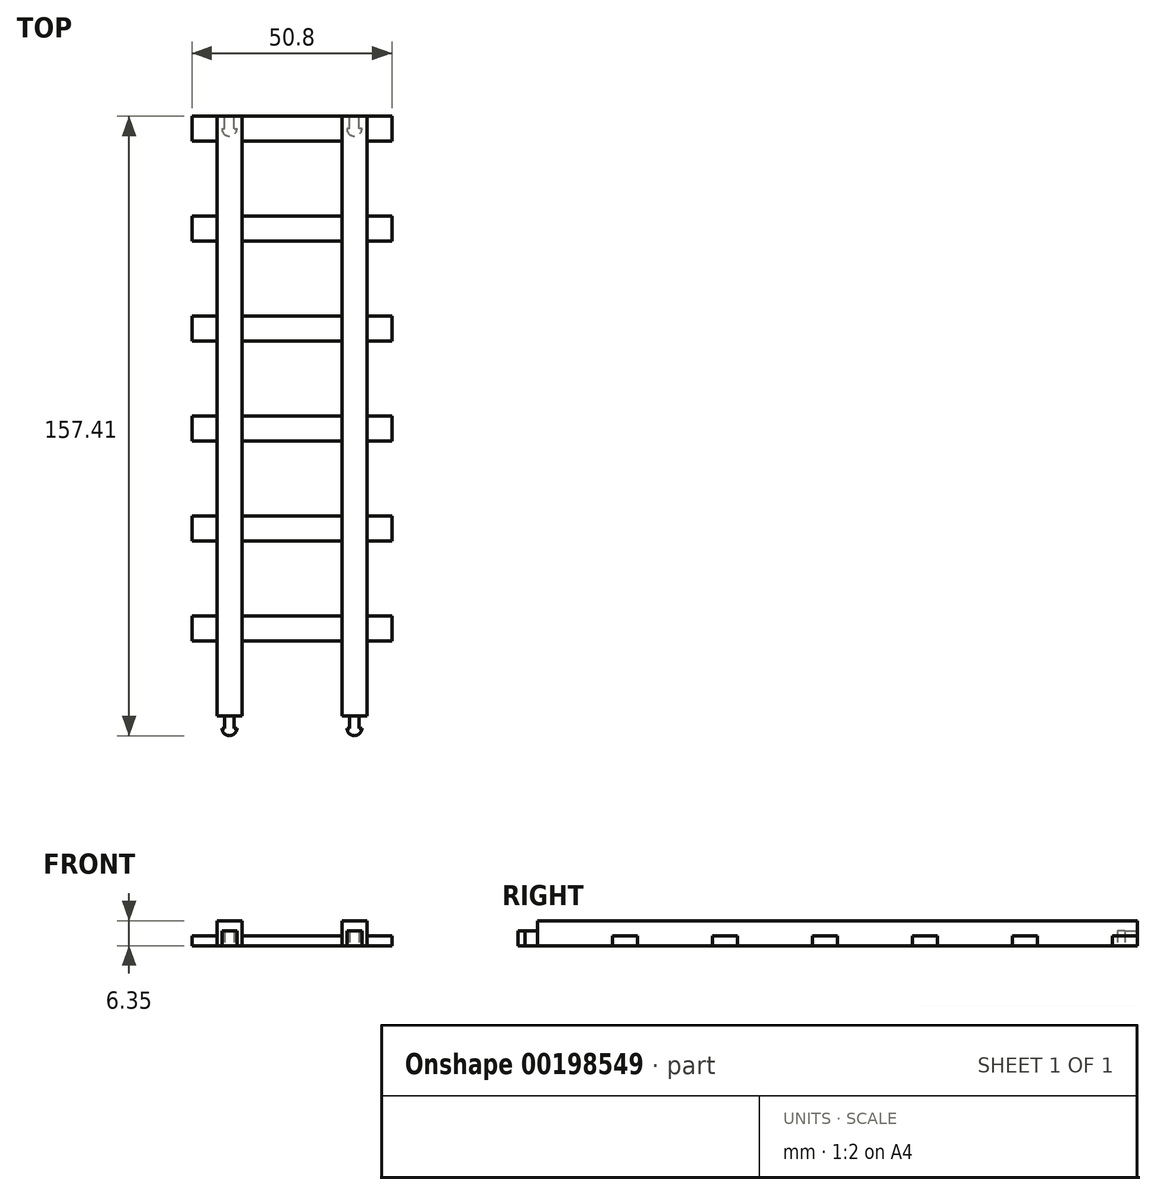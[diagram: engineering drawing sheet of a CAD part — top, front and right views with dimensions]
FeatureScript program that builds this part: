
annotation { "Feature Type Name" : "Feature", "Feature Type Description" : "" }
export const myFeature = defineFeature(function(context is Context, id is Id, definition is map)
    precondition{}
    {
        {
            var Q0;
            Q0=qCreatedBy(makeId("Top.planeOp"),FACE);
            var sketch = newSketch(context, id + "F0", { "sketchPlane" : qUnion([Q0])});
            skLineSegment(sketch, "E0.bottom", {"start": v(25.4, 76.2) * mm, "end": v(-25.4, 76.2) * mm, "construction": true});
            skLineSegment(sketch, "E0.top", {"start": v(25.4, -76.2) * mm, "end": v(-25.4, -76.2) * mm, "construction": true});
            skLineSegment(sketch, "E0.left", {"start": v(25.4, 76.2) * mm, "end": v(25.4, -76.2) * mm, "construction": true});
            skLineSegment(sketch, "E0.right", {"start": v(-25.4, 76.2) * mm, "end": v(-25.4, -76.2) * mm, "construction": true});
            skPoint(sketch, "E0.middle", {"position": v(0, 0) * mm});
            skLineSegment(sketch, "E1", {"start": v(-25.4, -76.2) * mm, "end": v(-19.05, -76.2) * mm, "construction": true});
            skLineSegment(sketch, "E2", {"start": v(-19.05, -76.2) * mm, "end": v(-19.05, 76.2) * mm});
            skLineSegment(sketch, "E3.MirrorCS", {"start": v(19.05, -76.2) * mm, "end": v(19.05, 76.2) * mm});
            skLineSegment(sketch, "E4", {"start": v(-25.4, -76.2) * mm, "end": v(-12.7, -76.2) * mm, "construction": true});
            skLineSegment(sketch, "E5", {"start": v(-12.7, -76.2) * mm, "end": v(-12.7, 76.2) * mm});
            skLineSegment(sketch, "E6.MirrorCS", {"start": v(12.7, -76.2) * mm, "end": v(12.7, 76.2) * mm});
            skLineSegment(sketch, "E7", {"start": v(-19.05, 76.2) * mm, "end": v(-12.7, 76.2) * mm});
            skLineSegment(sketch, "E8", {"start": v(12.7, 76.2) * mm, "end": v(19.05, 76.2) * mm});
            skLineSegment(sketch, "E9", {"start": v(-19.05, -76.2) * mm, "end": v(-12.7, -76.2) * mm});
            skLineSegment(sketch, "E10", {"start": v(12.7, -76.2) * mm, "end": v(19.05, -76.2) * mm});
            skSolve(sketch);
        }
        {
            var Q0;
            Q0 = qSketchRegion(id + "F0", true);
            extrude(context, id + "F1", {"entities" : qUnion([Q0]), "depth" : 6.35 * mm});
        }
        {
            var Q0;
            Q0=qCreatedBy(makeId("Top.planeOp"),FACE);
            var sketch = newSketch(context, id + "F2", { "sketchPlane" : qUnion([Q0])});
            skLineSegment(sketch, "E11.bottom", {"start": v(-25.4, -76.2) * mm, "end": v(25.4, -76.2) * mm, "construction": true});
            skLineSegment(sketch, "E11.top", {"start": v(-25.4, 76.2) * mm, "end": v(25.4, 76.2) * mm, "construction": true});
            skLineSegment(sketch, "E11.left", {"start": v(-25.4, -76.2) * mm, "end": v(-25.4, 76.2) * mm, "construction": true});
            skLineSegment(sketch, "E11.right", {"start": v(25.4, -76.2) * mm, "end": v(25.4, 76.2) * mm, "construction": true});
            skPoint(sketch, "E11.middle", {"position": v(0, 0) * mm});
            skLineSegment(sketch, "E12", {"start": v(-25.4, -76.2) * mm, "end": v(-25.4, -50.8) * mm, "construction": true});
            skLineSegment(sketch, "E13", {"start": v(-25.4, -76.2) * mm, "end": v(-25.4, -57.15) * mm, "construction": true});
            skLineSegment(sketch, "E14", {"start": v(-25.4, -57.15) * mm, "end": v(-25.4, -50.8) * mm});
            skLineSegment(sketch, "E15", {"start": v(-25.4, -50.8) * mm, "end": v(25.4, -50.8) * mm});
            skLineSegment(sketch, "E16", {"start": v(25.4, -50.8) * mm, "end": v(25.4, -57.15) * mm});
            skLineSegment(sketch, "E17", {"start": v(-25.4, -57.15) * mm, "end": v(25.4, -57.15) * mm});
            skLineSegment(sketch, "E18.0.1.0", {"start": v(-25.4, -25.4) * mm, "end": v(25.4, -25.4) * mm});
            skLineSegment(sketch, "E18.0.1.1", {"start": v(-25.4, -31.75) * mm, "end": v(25.4, -31.75) * mm});
            skLineSegment(sketch, "E18.0.1.2", {"start": v(25.4, -25.4) * mm, "end": v(25.4, -31.75) * mm});
            skLineSegment(sketch, "E18.0.1.3", {"start": v(-25.4, -31.75) * mm, "end": v(-25.4, -25.4) * mm});
            skLineSegment(sketch, "E18.0.2.0", {"start": v(-25.4, 0) * mm, "end": v(25.4, 0) * mm});
            skLineSegment(sketch, "E18.0.2.1", {"start": v(-25.4, -6.35) * mm, "end": v(25.4, -6.35) * mm});
            skLineSegment(sketch, "E18.0.2.2", {"start": v(25.4, 0) * mm, "end": v(25.4, -6.35) * mm});
            skLineSegment(sketch, "E18.0.2.3", {"start": v(-25.4, -6.35) * mm, "end": v(-25.4, 0) * mm});
            skLineSegment(sketch, "E18.0.3.0", {"start": v(-25.4, 25.4) * mm, "end": v(25.4, 25.4) * mm});
            skLineSegment(sketch, "E18.0.3.1", {"start": v(-25.4, 19.05) * mm, "end": v(25.4, 19.05) * mm});
            skLineSegment(sketch, "E18.0.3.2", {"start": v(25.4, 25.4) * mm, "end": v(25.4, 19.05) * mm});
            skLineSegment(sketch, "E18.0.3.3", {"start": v(-25.4, 19.05) * mm, "end": v(-25.4, 25.4) * mm});
            skLineSegment(sketch, "E18.0.4.0", {"start": v(-25.4, 50.8) * mm, "end": v(25.4, 50.8) * mm});
            skLineSegment(sketch, "E18.0.4.1", {"start": v(-25.4, 44.45) * mm, "end": v(25.4, 44.45) * mm});
            skLineSegment(sketch, "E18.0.4.2", {"start": v(25.4, 50.8) * mm, "end": v(25.4, 44.45) * mm});
            skLineSegment(sketch, "E18.0.4.3", {"start": v(-25.4, 44.45) * mm, "end": v(-25.4, 50.8) * mm});
            skLineSegment(sketch, "E18.0.5.0", {"start": v(-25.4, 76.2) * mm, "end": v(25.4, 76.2) * mm});
            skLineSegment(sketch, "E18.0.5.1", {"start": v(-25.4, 69.85) * mm, "end": v(25.4, 69.85) * mm});
            skLineSegment(sketch, "E18.0.5.2", {"start": v(25.4, 76.2) * mm, "end": v(25.4, 69.85) * mm});
            skLineSegment(sketch, "E18.0.5.3", {"start": v(-25.4, 69.85) * mm, "end": v(-25.4, 76.2) * mm});
            skLineSegment(sketch, "E18.direction1", {"start": v(-25.4, -50.8) * mm, "end": v(0, -50.8) * mm, "construction": true});
            skLineSegment(sketch, "E18.direction2", {"start": v(-25.4, -50.8) * mm, "end": v(-25.4, -25.4) * mm, "construction": true});
            skSolve(sketch);
        }
        {
            var Q0;
            Q0 = qSketchRegion(id + "F2", true);
            extrude(context, id + "F3", {"entities" : qUnion([Q0]), "operationType" : NewBodyOperationType.ADD, "depth" : 2.54 * mm});
        }
        {
            var Q0;
            Q0=makeQuery(id+"F3.boolean.opBoolean","MERGE",FACE,{"derivedFrom":[makeQuery(id+"F1.opExtrude","CAP_FACE",FACE,{"disambiguationData":[OSD([sQuery(id+"F0.wireOp",EDGE,"E2"),sQuery(id+"F0.wireOp",EDGE,"E5"),sQuery(id+"F0.wireOp",EDGE,"E7"),sQuery(id+"F0.wireOp",EDGE,"E9")])],"isStart":true}),makeQuery(id+"F1.opExtrude","CAP_FACE",FACE,{"disambiguationData":[OSD([sQuery(id+"F0.wireOp",EDGE,"E3.MirrorCS"),sQuery(id+"F0.wireOp",EDGE,"E6.MirrorCS"),sQuery(id+"F0.wireOp",EDGE,"E8"),sQuery(id+"F0.wireOp",EDGE,"E10")])],"isStart":true}),makeQuery(id+"F3.opExtrude","CAP_FACE",FACE,{"disambiguationData":[OSD([sQuery(id+"F2.wireOp",EDGE,"E14"),sQuery(id+"F2.wireOp",EDGE,"E15"),sQuery(id+"F2.wireOp",EDGE,"E16"),sQuery(id+"F2.wireOp",EDGE,"E17")])],"isStart":true}),makeQuery(id+"F3.opExtrude","CAP_FACE",FACE,{"disambiguationData":[OSD([sQuery(id+"F2.wireOp",EDGE,"E18.0.1.0"),sQuery(id+"F2.wireOp",EDGE,"E18.0.1.1"),sQuery(id+"F2.wireOp",EDGE,"E18.0.1.2"),sQuery(id+"F2.wireOp",EDGE,"E18.0.1.3")])],"isStart":true}),makeQuery(id+"F3.opExtrude","CAP_FACE",FACE,{"disambiguationData":[OSD([sQuery(id+"F2.wireOp",EDGE,"E18.0.2.0"),sQuery(id+"F2.wireOp",EDGE,"E18.0.2.1"),sQuery(id+"F2.wireOp",EDGE,"E18.0.2.2"),sQuery(id+"F2.wireOp",EDGE,"E18.0.2.3")])],"isStart":true}),makeQuery(id+"F3.opExtrude","CAP_FACE",FACE,{"disambiguationData":[OSD([sQuery(id+"F2.wireOp",EDGE,"E18.0.3.0"),sQuery(id+"F2.wireOp",EDGE,"E18.0.3.1"),sQuery(id+"F2.wireOp",EDGE,"E18.0.3.2"),sQuery(id+"F2.wireOp",EDGE,"E18.0.3.3")])],"isStart":true}),makeQuery(id+"F3.opExtrude","CAP_FACE",FACE,{"disambiguationData":[OSD([sQuery(id+"F2.wireOp",EDGE,"E18.0.4.0"),sQuery(id+"F2.wireOp",EDGE,"E18.0.4.1"),sQuery(id+"F2.wireOp",EDGE,"E18.0.4.2"),sQuery(id+"F2.wireOp",EDGE,"E18.0.4.3")])],"isStart":true}),makeQuery(id+"F3.opExtrude","CAP_FACE",FACE,{"disambiguationData":[OSD([sQuery(id+"F2.wireOp",EDGE,"E18.0.5.0"),sQuery(id+"F2.wireOp",EDGE,"E18.0.5.1"),sQuery(id+"F2.wireOp",EDGE,"E18.0.5.2"),sQuery(id+"F2.wireOp",EDGE,"E18.0.5.3")])],"isStart":true})]});
            var sketch = newSketch(context, id + "F4", { "sketchPlane" : qUnion([Q0])});
            skLineSegment(sketch, "E19", {"start": v(19.05, -76.2) * mm, "end": v(19.05, -69.85) * mm, "construction": true});
            skLineSegment(sketch, "E20", {"start": v(19.05, -69.85) * mm, "end": v(12.7, -69.85) * mm, "construction": true});
            skLineSegment(sketch, "E21", {"start": v(12.7, -69.85) * mm, "end": v(12.7, -76.2) * mm, "construction": true});
            skLineSegment(sketch, "E22", {"start": v(12.7, -73.02) * mm, "end": v(19.05, -73.02) * mm, "construction": true});
            skLineSegment(sketch, "E23", {"start": v(15.87, -69.85) * mm, "end": v(15.87, -76.2) * mm, "construction": true});
            skCircle(sketch, "E24", {"center": v(15.87, -73.02) * mm, "radius": 1.9 * mm, "construction": true});
            skArc(sketch, "E25", {"start": v(17.78, -73.02) * mm, "mid": v(15.87, -71.12) * mm, "end": v(13.97, -73.02) * mm});
            skPoint(sketch, "E26", {"position": v(14.29, -69.85) * mm});
            skLineSegment(sketch, "E27", {"start": v(15.87, -69.85) * mm, "end": v(12.7, -69.85) * mm, "construction": true});
            skLineSegment(sketch, "E28", {"start": v(14.29, -69.85) * mm, "end": v(14.29, -76.2) * mm, "construction": true});
            skLineSegment(sketch, "E29.MirrorCS", {"start": v(17.46, -69.85) * mm, "end": v(17.46, -76.2) * mm, "construction": true});
            skLineSegment(sketch, "E30", {"start": v(14.29, -69.85) * mm, "end": v(15.87, -69.85) * mm, "construction": true});
            skPoint(sketch, "E31", {"position": v(15.08, -69.85) * mm});
            skLineSegment(sketch, "E32", {"start": v(15.08, -69.85) * mm, "end": v(15.08, -76.2) * mm, "construction": true});
            skLineSegment(sketch, "E33", {"start": v(14.29, -73.02) * mm, "end": v(15.08, -73.02) * mm, "construction": true});
            skPoint(sketch, "E34", {"position": v(14.68, -73.02) * mm});
            skLineSegment(sketch, "E35", {"start": v(14.68, -73.02) * mm, "end": v(14.68, -76.2) * mm});
            skLineSegment(sketch, "E36.MirrorCS", {"start": v(17.07, -73.02) * mm, "end": v(17.07, -76.2) * mm});
            skLineSegment(sketch, "E37", {"start": v(14.68, -73.02) * mm, "end": v(13.97, -73.02) * mm});
            skLineSegment(sketch, "E38", {"start": v(17.78, -73.02) * mm, "end": v(17.07, -73.02) * mm});
            skLineSegment(sketch, "E39", {"start": v(14.68, -76.2) * mm, "end": v(17.07, -76.2) * mm});
            skLineSegment(sketch, "E40.MirrorCS", {"start": v(-17.07, -73.02) * mm, "end": v(-17.07, -76.2) * mm});
            skLineSegment(sketch, "E41.MirrorCS", {"start": v(-14.68, -73.02) * mm, "end": v(-14.68, -76.2) * mm});
            skLineSegment(sketch, "E42.MirrorCS", {"start": v(-17.78, -73.02) * mm, "end": v(-17.07, -73.02) * mm});
            skArc(sketch, "E43.MirrorCS", {"start": v(-17.78, -73.02) * mm, "mid": v(-15.87, -71.12) * mm, "end": v(-13.97, -73.02) * mm});
            skLineSegment(sketch, "E44.MirrorCS", {"start": v(-14.68, -73.02) * mm, "end": v(-13.97, -73.02) * mm});
            skLineSegment(sketch, "E45.MirrorCS", {"start": v(-14.68, -76.2) * mm, "end": v(-17.07, -76.2) * mm});
            skSolve(sketch);
        }
        {
            var Q0;
            Q0 = qSketchRegion(id + "F4", true);
            extrude(context, id + "F5", {"entities" : qUnion([Q0]), "operationType" : NewBodyOperationType.REMOVE, "oppositeDirection" : true, "depth" : 3.8 * mm});
        }
        {
            var Q0;
            Q0=makeQuery(id+"F3.boolean.opBoolean","MERGE",FACE,{"derivedFrom":[makeQuery(id+"F1.opExtrude","CAP_FACE",FACE,{"disambiguationData":[OSD([sQuery(id+"F0.wireOp",EDGE,"E2"),sQuery(id+"F0.wireOp",EDGE,"E5"),sQuery(id+"F0.wireOp",EDGE,"E7"),sQuery(id+"F0.wireOp",EDGE,"E9")])],"isStart":true}),makeQuery(id+"F1.opExtrude","CAP_FACE",FACE,{"disambiguationData":[OSD([sQuery(id+"F0.wireOp",EDGE,"E3.MirrorCS"),sQuery(id+"F0.wireOp",EDGE,"E6.MirrorCS"),sQuery(id+"F0.wireOp",EDGE,"E8"),sQuery(id+"F0.wireOp",EDGE,"E10")])],"isStart":true}),makeQuery(id+"F3.opExtrude","CAP_FACE",FACE,{"disambiguationData":[OSD([sQuery(id+"F2.wireOp",EDGE,"E14"),sQuery(id+"F2.wireOp",EDGE,"E15"),sQuery(id+"F2.wireOp",EDGE,"E16"),sQuery(id+"F2.wireOp",EDGE,"E17")])],"isStart":true}),makeQuery(id+"F3.opExtrude","CAP_FACE",FACE,{"disambiguationData":[OSD([sQuery(id+"F2.wireOp",EDGE,"E18.0.1.0"),sQuery(id+"F2.wireOp",EDGE,"E18.0.1.1"),sQuery(id+"F2.wireOp",EDGE,"E18.0.1.2"),sQuery(id+"F2.wireOp",EDGE,"E18.0.1.3")])],"isStart":true}),makeQuery(id+"F3.opExtrude","CAP_FACE",FACE,{"disambiguationData":[OSD([sQuery(id+"F2.wireOp",EDGE,"E18.0.2.0"),sQuery(id+"F2.wireOp",EDGE,"E18.0.2.1"),sQuery(id+"F2.wireOp",EDGE,"E18.0.2.2"),sQuery(id+"F2.wireOp",EDGE,"E18.0.2.3")])],"isStart":true}),makeQuery(id+"F3.opExtrude","CAP_FACE",FACE,{"disambiguationData":[OSD([sQuery(id+"F2.wireOp",EDGE,"E18.0.3.0"),sQuery(id+"F2.wireOp",EDGE,"E18.0.3.1"),sQuery(id+"F2.wireOp",EDGE,"E18.0.3.2"),sQuery(id+"F2.wireOp",EDGE,"E18.0.3.3")])],"isStart":true}),makeQuery(id+"F3.opExtrude","CAP_FACE",FACE,{"disambiguationData":[OSD([sQuery(id+"F2.wireOp",EDGE,"E18.0.4.0"),sQuery(id+"F2.wireOp",EDGE,"E18.0.4.1"),sQuery(id+"F2.wireOp",EDGE,"E18.0.4.2"),sQuery(id+"F2.wireOp",EDGE,"E18.0.4.3")])],"isStart":true}),makeQuery(id+"F3.opExtrude","CAP_FACE",FACE,{"disambiguationData":[OSD([sQuery(id+"F2.wireOp",EDGE,"E18.0.5.0"),sQuery(id+"F2.wireOp",EDGE,"E18.0.5.1"),sQuery(id+"F2.wireOp",EDGE,"E18.0.5.2"),sQuery(id+"F2.wireOp",EDGE,"E18.0.5.3")])],"isStart":true})]});
            var sketch = newSketch(context, id + "F6", { "sketchPlane" : qUnion([Q0])});
            skLineSegment(sketch, "E46", {"start": v(-15.88, 76.2) * mm, "end": v(-15.88, 79.38) * mm, "construction": true});
            skLineSegment(sketch, "E47", {"start": v(-15.88, 76.2) * mm, "end": v(-17.06, 76.2) * mm});
            skLineSegment(sketch, "E48.MirrorCS", {"start": v(-15.88, 76.2) * mm, "end": v(-14.69, 76.2) * mm});
            skLineSegment(sketch, "E49", {"start": v(-17.06, 76.2) * mm, "end": v(-17.06, 79.38) * mm});
            skLineSegment(sketch, "E50", {"start": v(-17.06, 79.38) * mm, "end": v(-17.78, 79.38) * mm});
            skLineSegment(sketch, "E51.MirrorCS", {"start": v(-14.69, 76.2) * mm, "end": v(-14.69, 79.38) * mm});
            skLineSegment(sketch, "E52.MirrorCS", {"start": v(-14.69, 79.38) * mm, "end": v(-13.97, 79.38) * mm});
            skArc(sketch, "E53", {"start": v(-13.97, 79.38) * mm, "mid": v(-15.88, 81.21) * mm, "end": v(-17.78, 79.38) * mm});
            skArc(sketch, "E54.MirrorCS", {"start": v(13.97, 79.38) * mm, "mid": v(15.88, 81.21) * mm, "end": v(17.78, 79.38) * mm});
            skLineSegment(sketch, "E55.MirrorCS", {"start": v(17.06, 79.38) * mm, "end": v(17.78, 79.38) * mm});
            skLineSegment(sketch, "E56.MirrorCS", {"start": v(14.69, 79.38) * mm, "end": v(13.97, 79.38) * mm});
            skLineSegment(sketch, "E57.MirrorCS", {"start": v(14.69, 76.2) * mm, "end": v(14.69, 79.38) * mm});
            skLineSegment(sketch, "E58.MirrorCS", {"start": v(17.06, 76.2) * mm, "end": v(17.06, 79.38) * mm});
            skLineSegment(sketch, "E59.MirrorCS", {"start": v(15.88, 76.2) * mm, "end": v(17.06, 76.2) * mm});
            skLineSegment(sketch, "E60.MirrorCS", {"start": v(15.88, 76.2) * mm, "end": v(14.69, 76.2) * mm});
            skSolve(sketch);
        }
        {
            var Q0;
            Q0 = qSketchRegion(id + "F6", true);
            extrude(context, id + "F7", {"entities" : qUnion([Q0]), "operationType" : NewBodyOperationType.ADD, "oppositeDirection" : true, "depth" : 3.8 * mm});
        }
    });
